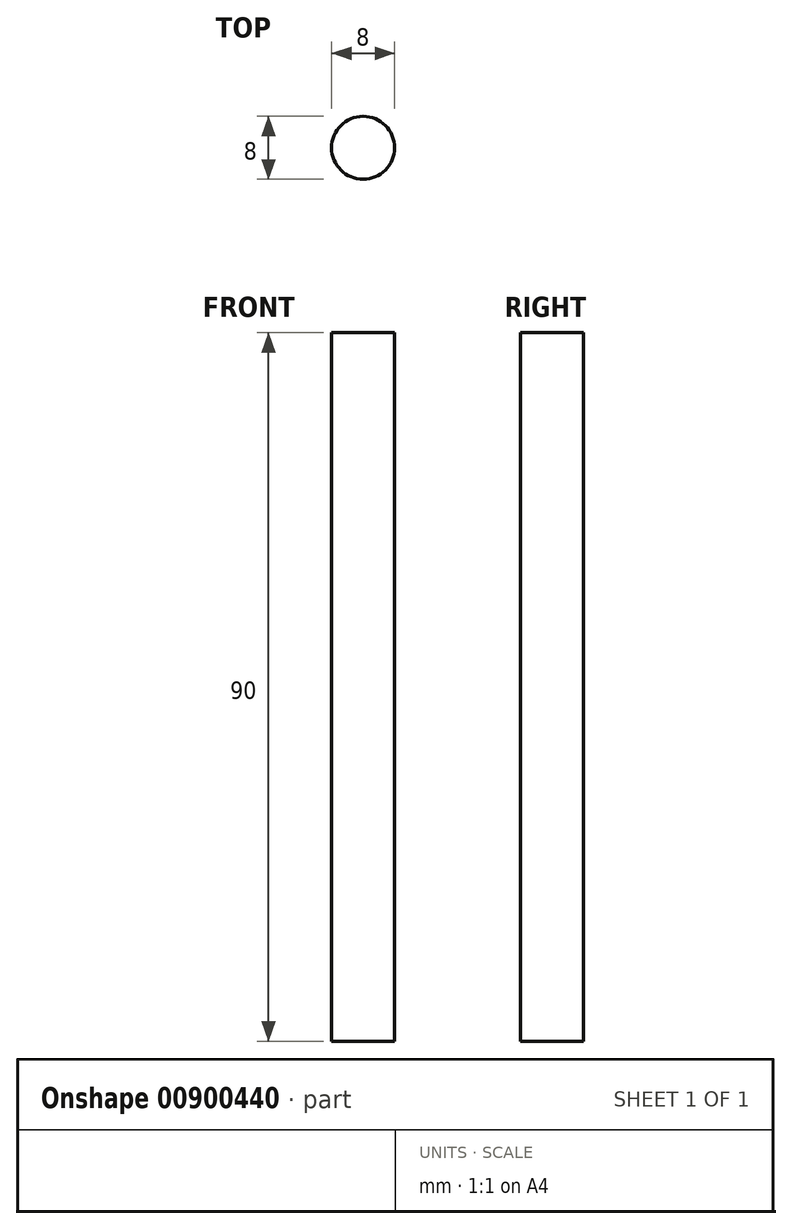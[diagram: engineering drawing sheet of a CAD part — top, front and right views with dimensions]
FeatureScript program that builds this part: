
annotation { "Feature Type Name" : "Feature", "Feature Type Description" : "" }
export const myFeature = defineFeature(function(context is Context, id is Id, definition is map)
    precondition{}
    {
        {
            var Q0;
            Q0=qCreatedBy(makeId("Top.planeOp"),FACE);
            var sketch = newSketch(context, id + "F0", { "sketchPlane" : qUnion([Q0])});
            skCircle(sketch, "E0", {"center": v(0, 0) * mm, "radius": 4 * mm});
            skSolve(sketch);
        }
        {
            var Q0;
            Q0 = qSketchRegion(id + "F0", true);
            extrude(context, id + "F1", {"entities" : qUnion([Q0]), "depth" : 90 * mm, "offsetDistance" : 25 * mm});
        }
    });
